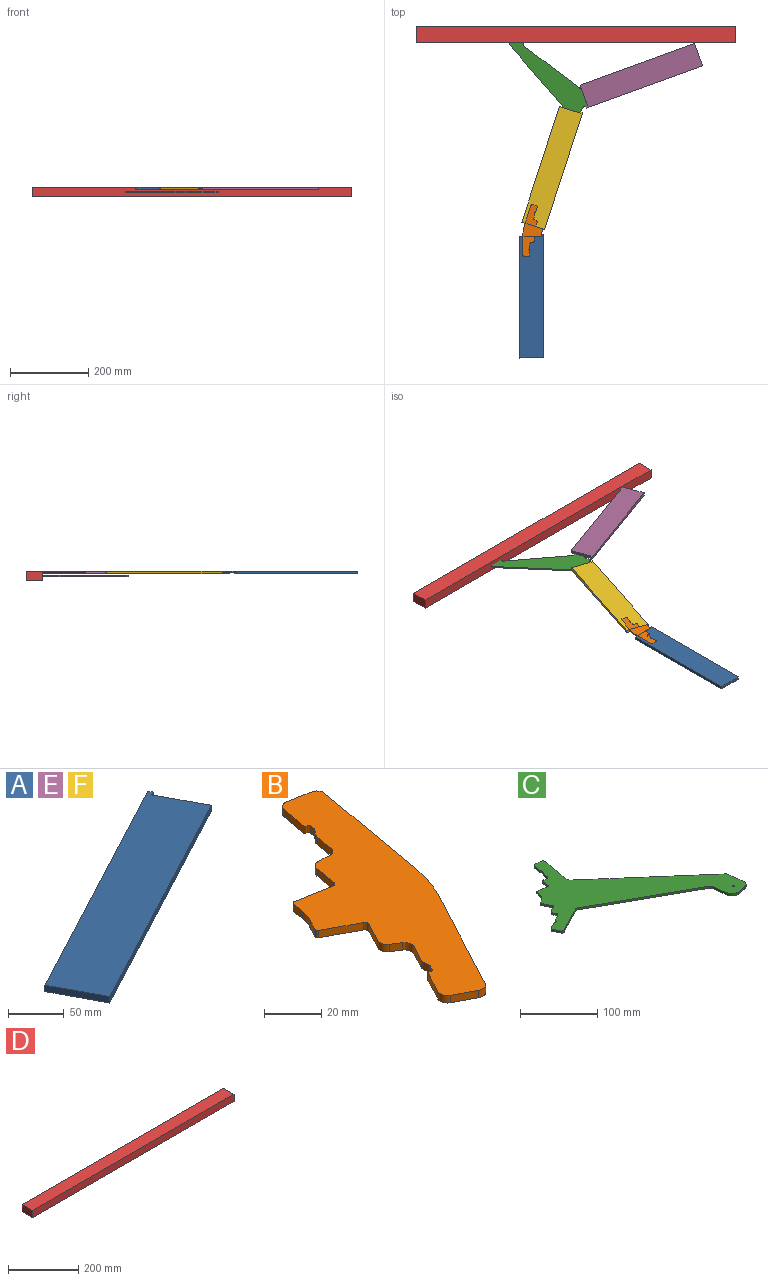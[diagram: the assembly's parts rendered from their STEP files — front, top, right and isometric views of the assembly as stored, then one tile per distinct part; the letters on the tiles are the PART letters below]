
ASSEMBLY  parts=6 mates=11
PART A: 8 faces, bbox 302.3x201.4x7 mm
  f0: plane 273.71x145.54mm, normal (0.47,-0.88,0), area 2170mm2, adj f1,f5,f6,f7
  f1: plane 53.7x28.55mm, normal (-0.88,-0.47,0), area 425.7mm2, adj f0,f2,f6,f7
  f2: plane 277.81x147.71mm, normal (-0.47,0.88,0), area 2202.5mm2, adj f1,f3,f6,f7
  f3: plane 7x4.72mm, normal (0.88,0.47,0), area 37.4mm2, adj f2,f4,f6,f7
  f4: plane 7x4.1mm, normal (0.47,-0.88,0), area 32.5mm2, adj f3,f5,f6,f7
  f5: plane 48.98x26.04mm, normal (0.88,0.47,0), area 388.3mm2, adj f0,f4,f6,f7
  f6: plane 302.26x201.41mm, normal (0,0,-1), area 18877.3mm2, adj f0,f1,f2,f3,f4,f5
  f7: plane 302.26x201.41mm, normal (0,0,1), area 18877.3mm2, adj f0,f1,f2,f3,f4,f5
PART B: 46 faces, bbox 61x129x3.2 mm
  f0: plane 5.41x3.18mm, normal (-0.98,0.17,0), area 17.4mm2, adj f1,f42,f43,f45
  f1: cylinder r=1.02mm len=3.18mm, axis (0,0,1), area 5.1mm2, adj f0,f2,f42,f43
  f2: plane 16.13x3.18mm, normal (0.17,0.98,0), area 52mm2, adj f1,f3,f42,f43
  f3: cylinder r=1.65mm len=3.18mm, axis (0,0,1), area 8.2mm2, adj f2,f4,f42,f43
  f4: plane 10.09x3.18mm, normal (-0.98,0.17,0), area 32.5mm2, adj f3,f5,f42,f43
  f5: cylinder r=3.43mm len=3.68mm, axis (0,0,1), area 16.2mm2, adj f4,f6,f42,f43
  f6: plane 4.85x3.18mm, normal (0.09,1,0), area 15.5mm2, adj f5,f7,f42,f43
  f7: cylinder r=3.43mm len=3.68mm, axis (0,0,1), area 16.2mm2, adj f6,f8,f42,f43
  f8: plane 8.7x3.18mm, normal (-0.98,0.17,0), area 28mm2, adj f7,f9,f42,f43
  f9: cylinder r=1.6mm len=3.18mm, axis (0,0,1), area 2.6mm2, adj f8,f10,f42,f43
  f10: plane 3.18x2.65mm, normal (-0.78,0.63,0), area 10.8mm2, adj f9,f11,f42,f43
  f11: cylinder r=1.6mm len=3.18mm, axis (0,0,1), area 2.6mm2, adj f10,f12,f42,f43
  f12: plane 3.18x1.85mm, normal (-0.98,0.17,0), area 6mm2, adj f11,f13,f42,f43
  f13: cylinder r=0.89mm len=3.18mm, axis (0,0,1), area 4.4mm2, adj f12,f14,f42,f43
  f14: plane 3.18x0.63mm, normal (-0.17,-0.98,0), area 2mm2, adj f13,f15,f42,f43
  f15: cylinder r=0.51mm len=3.18mm, axis (0,0,1), area 2.5mm2, adj f14,f16,f42,f43
  f16: plane 11.79x3.18mm, normal (-0.98,0.17,0), area 38mm2, adj f15,f17,f42,f43
  f17: cylinder r=3.43mm len=3.97mm, axis (0,0,1), area 17.1mm2, adj f16,f18,f42,f43
  f18: plane 10.29x3.18mm, normal (0.17,0.98,0), area 33.2mm2, adj f17,f19,f42,f43
  f19: cylinder r=3.43mm len=3.97mm, axis (0,0,1), area 17.1mm2, adj f18,f20,f42,f43
  f20: plane 55.38x9.77mm, normal (0.98,-0.17,0), area 178.6mm2, adj f19,f42,f43,f44
  f21: plane 49.66x26.4mm, normal (0.88,-0.47,0), area 178.6mm2, adj f22,f42,f43,f44
  f22: cylinder r=3.43mm len=4.64mm, axis (0,0,1), area 17.1mm2, adj f21,f23,f42,f43
  f23: plane 9.23x4.91mm, normal (-0.47,-0.88,0), area 33.2mm2, adj f22,f24,f42,f43
  f24: cylinder r=3.43mm len=4.64mm, axis (0,0,1), area 17.1mm2, adj f23,f25,f42,f43
  f25: plane 10.57x5.62mm, normal (-0.88,0.47,0), area 38mm2, adj f24,f26,f42,f43
  f26: cylinder r=0.51mm len=3.18mm, axis (0,0,1), area 2.5mm2, adj f25,f27,f42,f43
  f27: plane 3.18x0.56mm, normal (0.47,0.88,0), area 2mm2, adj f26,f28,f42,f43
  f28: cylinder r=0.89mm len=3.18mm, axis (0,0,1), area 4.4mm2, adj f27,f29,f42,f43
  f29: plane 3.18x1.66mm, normal (-0.88,0.47,0), area 6mm2, adj f28,f30,f42,f43
  f30: cylinder r=1.6mm len=3.18mm, axis (0,0,1), area 2.6mm2, adj f29,f31,f42,f43
  f31: plane 3.4x3.18mm, normal (-1,-0.01,0), area 10.8mm2, adj f30,f32,f42,f43
  f32: cylinder r=1.6mm len=3.18mm, axis (0,0,1), area 2.6mm2, adj f31,f33,f42,f43
  f33: plane 7.8x4.15mm, normal (-0.88,0.47,0), area 28mm2, adj f32,f34,f42,f43
  f34: cylinder r=3.43mm len=4.49mm, axis (0,0,1), area 16.2mm2, adj f33,f35,f42,f43
  f35: plane 4.09x3.18mm, normal (-0.54,-0.84,0), area 15.5mm2, adj f34,f36,f42,f43
  f36: cylinder r=3.43mm len=4.49mm, axis (0,0,1), area 16.2mm2, adj f35,f37,f42,f43
  f37: plane 9.04x4.81mm, normal (-0.88,0.47,0), area 32.5mm2, adj f36,f38,f42,f43
  f38: cylinder r=1.65mm len=3.18mm, axis (0,0,1), area 8.2mm2, adj f37,f39,f42,f43
  f39: plane 14.47x7.69mm, normal (-0.47,-0.88,0), area 52mm2, adj f38,f40,f42,f43
  f40: cylinder r=1.02mm len=3.18mm, axis (0,0,1), area 5.1mm2, adj f39,f41,f42,f43
  f41: plane 4.85x3.18mm, normal (-0.88,0.47,0), area 17.4mm2, adj f40,f42,f43,f45
  f42: plane 128.97x60.96mm, normal (0,0,-1), area 3359.7mm2, adj f0,f1,f2,f3,f4,f5,f6,f7
  f43: plane 128.97x60.96mm, normal (0,0,1), area 3359.7mm2, adj f0,f1,f2,f3,f4,f5,f6,f7
  f44: cylinder r=55mm len=16.27mm, axis (0,0,-1), area 54.9mm2, adj f20,f21,f42,f43
  f45: cylinder r=20mm len=5.92mm, axis (0,0,1), area 19.9mm2, adj f0,f41,f42,f43
PART C: 57 faces, bbox 250.7x229.8x3.2 mm
  f0: plane 4.29x3.18mm, normal (-0.98,0.17,0), area 13.8mm2, adj f1,f48,f49,f50
  f1: cylinder r=1.02mm len=3.18mm, axis (0,0,1), area 5.1mm2, adj f0,f2,f48,f49
  f2: plane 16.13x3.18mm, normal (0.17,0.98,0), area 52mm2, adj f1,f3,f48,f49
  f3: cylinder r=1.65mm len=3.18mm, axis (0,0,1), area 8.2mm2, adj f2,f4,f48,f49
  f4: plane 10.09x3.18mm, normal (-0.98,0.17,0), area 32.5mm2, adj f3,f5,f48,f49
  f5: cylinder r=3.43mm len=3.68mm, axis (0,0,1), area 16.2mm2, adj f4,f6,f48,f49
  f6: plane 4.85x3.18mm, normal (0.09,1,0), area 15.5mm2, adj f5,f7,f48,f49
  f7: cylinder r=3.43mm len=3.68mm, axis (0,0,1), area 16.2mm2, adj f6,f8,f48,f49
  f8: plane 8.7x3.18mm, normal (-0.98,0.17,0), area 28mm2, adj f7,f9,f48,f49
  f9: cylinder r=1.6mm len=3.18mm, axis (0,0,1), area 2.6mm2, adj f8,f10,f48,f49
  f10: plane 3.18x2.65mm, normal (-0.78,0.63,0), area 10.8mm2, adj f9,f11,f48,f49
  f11: cylinder r=1.6mm len=3.18mm, axis (0,0,1), area 2.6mm2, adj f10,f12,f48,f49
  f12: plane 3.18x1.85mm, normal (-0.98,0.17,0), area 6mm2, adj f11,f13,f48,f49
  f13: cylinder r=0.89mm len=3.18mm, axis (0,0,1), area 4.4mm2, adj f12,f14,f48,f49
  f14: plane 3.18x0.63mm, normal (-0.17,-0.98,0), area 2mm2, adj f13,f15,f48,f49
  f15: cylinder r=0.51mm len=3.18mm, axis (0,0,1), area 2.5mm2, adj f14,f16,f48,f49
  f16: plane 11.79x3.18mm, normal (-0.98,0.17,0), area 38mm2, adj f15,f17,f48,f49
  f17: cylinder r=3.43mm len=3.97mm, axis (0,0,1), area 17.1mm2, adj f16,f18,f48,f49
  f18: plane 10.29x3.18mm, normal (0.17,0.98,0), area 33.2mm2, adj f17,f19,f48,f49
  f19: cylinder r=3.43mm len=3.97mm, axis (0,0,1), area 17.1mm2, adj f18,f20,f48,f49
  f20: plane 47.76x8.42mm, normal (0.98,-0.17,0), area 154mm2, adj f19,f48,f49,f53
  f21: plane 152.08x132.48mm, normal (0.66,0.75,0), area 640.4mm2, adj f48,f49,f53,f54
  f22: plane 24.27x3.41mm, normal (0.99,0.14,0), area 77.8mm2, adj f48,f49,f51,f54
  f23: plane 13.54x3.18mm, normal (0.14,-0.99,0), area 43.4mm2, adj f48,f49,f51,f52
  f24: plane 23.78x3.34mm, normal (-0.99,-0.14,0), area 76.2mm2, adj f48,f49,f52,f55
  f25: plane 155.2x86.3mm, normal (-0.49,-0.87,0), area 563.8mm2, adj f48,f49,f55,f56
  f26: plane 42.89x22.81mm, normal (0.47,-0.88,0), area 154.2mm2, adj f27,f48,f49,f56
  f27: cylinder r=3.43mm len=4.64mm, axis (0,0,1), area 17.1mm2, adj f26,f28,f48,f49
  f28: plane 9.23x4.91mm, normal (-0.88,-0.47,0), area 33.2mm2, adj f27,f29,f48,f49
  f29: cylinder r=3.43mm len=4.64mm, axis (0,0,1), area 17.1mm2, adj f28,f30,f48,f49
  f30: plane 10.57x5.62mm, normal (-0.47,0.88,0), area 38mm2, adj f29,f31,f48,f49
  f31: cylinder r=0.51mm len=3.18mm, axis (0,0,1), area 2.5mm2, adj f30,f32,f48,f49
  f32: plane 3.18x0.56mm, normal (0.88,0.47,0), area 2mm2, adj f31,f33,f48,f49
  f33: cylinder r=0.89mm len=3.18mm, axis (0,0,1), area 4.4mm2, adj f32,f34,f48,f49
  f34: plane 3.18x1.66mm, normal (-0.47,0.88,0), area 6mm2, adj f33,f35,f48,f49
  f35: cylinder r=1.6mm len=3.18mm, axis (0,0,1), area 2.6mm2, adj f34,f36,f48,f49
  f36: plane 3.18x2.84mm, normal (-0.84,0.55,0), area 10.8mm2, adj f35,f37,f48,f49
  f37: cylinder r=1.6mm len=3.18mm, axis (0,0,1), area 2.6mm2, adj f36,f38,f48,f49
  f38: plane 7.8x4.15mm, normal (-0.47,0.88,0), area 28mm2, adj f37,f39,f48,f49
  f39: cylinder r=3.43mm len=4.37mm, axis (0,0,1), area 16.2mm2, adj f38,f40,f48,f49
  f40: plane 4.48x3.18mm, normal (-0.92,-0.39,0), area 15.5mm2, adj f39,f41,f48,f49
  f41: cylinder r=3.43mm len=4.37mm, axis (0,0,1), area 16.2mm2, adj f40,f42,f48,f49
  f42: plane 9.04x4.81mm, normal (-0.47,0.88,0), area 32.5mm2, adj f41,f43,f48,f49
  f43: cylinder r=1.65mm len=3.18mm, axis (0,0,1), area 8.2mm2, adj f42,f44,f48,f49
  f44: plane 14.47x7.69mm, normal (-0.88,-0.47,0), area 52mm2, adj f43,f45,f48,f49
  f45: cylinder r=1.02mm len=3.18mm, axis (0,0,1), area 5.1mm2, adj f44,f46,f48,f49
  f46: plane 3.85x3.18mm, normal (-0.47,0.88,0), area 13.8mm2, adj f45,f48,f49,f50
  f47: cylinder r=1.25mm len=3.18mm, axis (0,0,1), area 24.9mm2, adj f48,f49
  f48: plane 250.66x229.81mm, normal (0,0,-1), area 13646.2mm2, adj f0,f1,f2,f3,f4,f5,f6,f7
  f49: plane 250.66x229.81mm, normal (0,0,1), area 13646.2mm2, adj f0,f1,f2,f3,f4,f5,f6,f7
  f50: cylinder r=20mm len=14.19mm, axis (0,0,1), area 57.6mm2, adj f0,f46,f48,f49
  f51: cylinder r=10mm len=11.29mm, axis (0,0,1), area 49.9mm2, adj f22,f23,f48,f49
  f52: cylinder r=10mm len=11.29mm, axis (0,0,-1), area 49.9mm2, adj f23,f24,f48,f49
  f53: cylinder r=4mm len=3.71mm, axis (0,0,-1), area 13.1mm2, adj f20,f21,f48,f49
  f54: cylinder r=4mm len=3.18mm, axis (0,0,1), area 9.1mm2, adj f21,f22,f48,f49
  f55: cylinder r=4mm len=3.18mm, axis (0,0,-1), area 11.7mm2, adj f24,f25,f48,f49
  f56: cylinder r=4mm len=3.82mm, axis (0,0,-1), area 12.7mm2, adj f25,f26,f48,f49
PART D: 6 faces, bbox 813.2x42.4x25 mm
  f0: plane 813.22x25mm, normal (0,1,0), area 20330.4mm2, adj f1,f3,f4,f5
  f1: plane 42.36x25mm, normal (-1,0,0), area 1059mm2, adj f0,f2,f4,f5
  f2: plane 813.22x25mm, normal (0,-1,0), area 20330.4mm2, adj f1,f3,f4,f5
  f3: plane 42.36x25mm, normal (1,0,0), area 1059mm2, adj f0,f2,f4,f5
  f4: plane 813.22x42.36mm, normal (0,0,1), area 34448.4mm2, adj f0,f1,f2,f3
  f5: plane 813.22x42.36mm, normal (0,0,-1), area 34448.4mm2, adj f0,f1,f2,f3
PART E: same geometry as A
PART F: same geometry as A
PLACE A rot(axis=(0.52,0.86,0),180deg) t=(60.01,476.87,-47.33)mm
PLACE B rot(axis=(0,0,-1),170deg) t=(199.66,763.2,-472.33)mm
PLACE C rot(axis=(0,0,1),172deg) t=(345.24,1050.54,-483.24)mm
PLACE D t=(185.38,1244.26,-281.33)mm fixed
PLACE E rot(axis=(0,0,1),172deg) t=(345.24,1050.54,-472.33)mm
PLACE F rot(axis=(0.64,0.77,0),180deg) t=(123.95,821.39,-47.33)mm
MATE planar E.f4 <-> C.f46  axis (-0.34,0.94,0) through (254.36,932.88,-259.83)mm
MATE planar E.f7 <-> D.f4  axis (0,0,1) through (393.44,1010.13,-256.33)mm
MATE planar F.f4 <-> C.f0  axis (-0.95,0.31,0) through (238.37,916.32,-259.83)mm
MATE planar F.f5 <-> C.f2  axis (0.31,0.95,0) through (211.27,922.68,-259.83)mm
MATE planar F.f6 <-> D.f4  axis (0,0,1) through (166.01,774.63,-256.33)mm
MATE planar B.f43 <-> D.f4  axis (0,0,1) through (111.02,614.39,-256.33)mm
MATE planar A.f5 <-> B.f2  axis (0,1,0) through (111.76,600.2,-259.83)mm
MATE planar A.f6 <-> D.f4  axis (0,0,1) through (114.46,445.4,-256.33)mm
MATE planar E.f5 <-> C.f44  axis (-0.94,-0.34,0) through (247.05,959.73,-259.83)mm
MATE planar B.f39 <-> F.f1  axis (0.31,0.95,0) through (133.73,621.93,-257.91)mm
MATE planar A.f4 <-> B.f0  axis (-1,0,0) through (139.49,602.52,-259.83)mm
